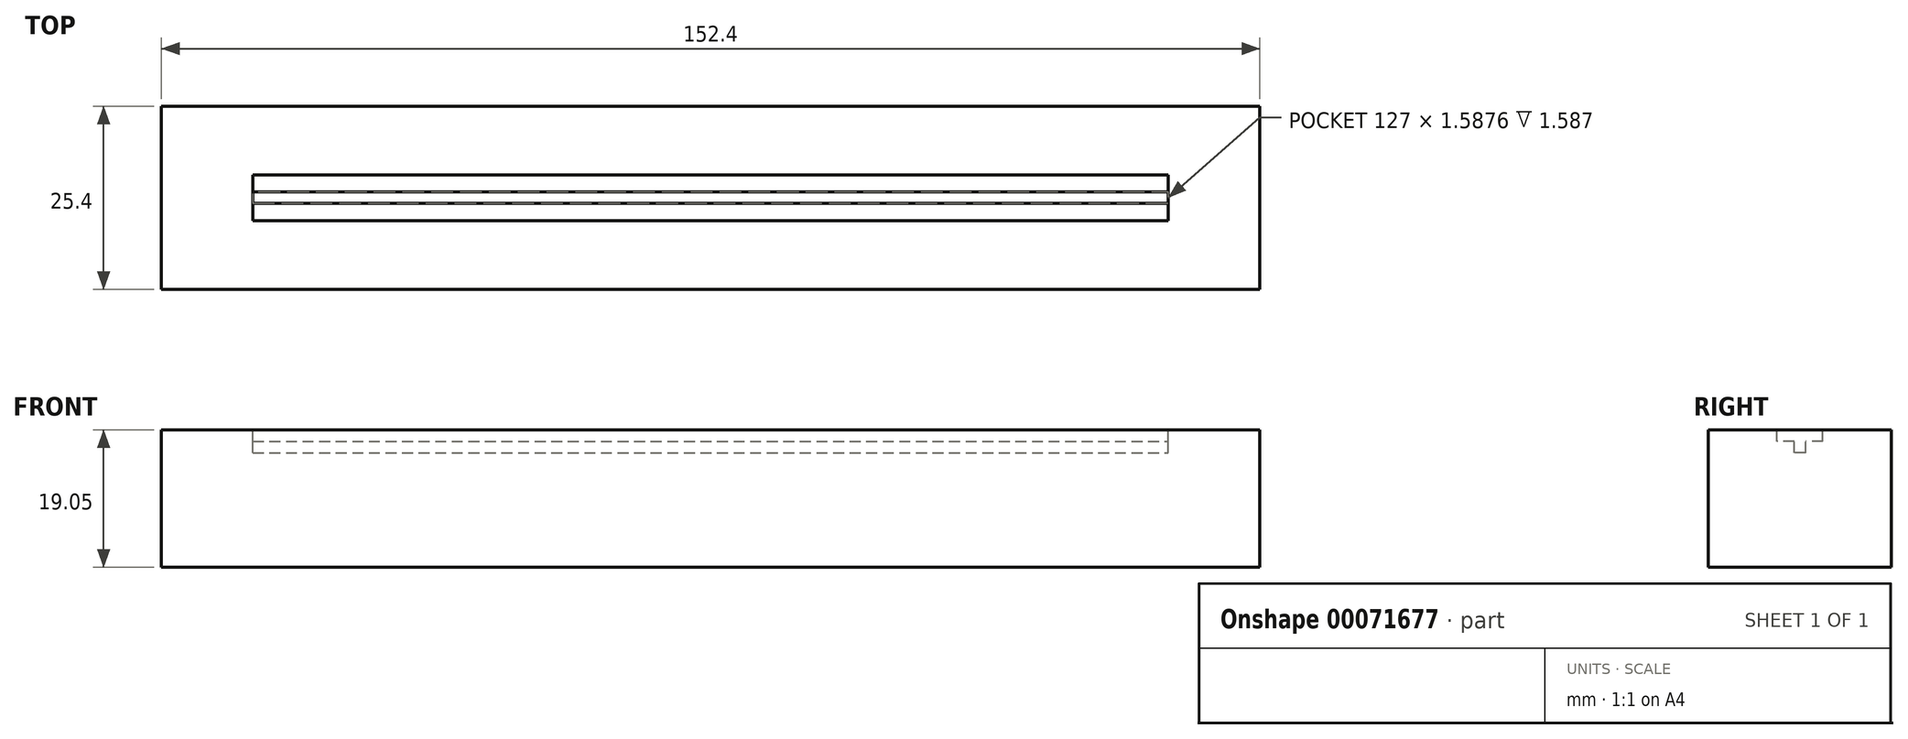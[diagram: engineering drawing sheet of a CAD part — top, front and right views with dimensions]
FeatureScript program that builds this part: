
annotation { "Feature Type Name" : "Feature", "Feature Type Description" : "" }
export const myFeature = defineFeature(function(context is Context, id is Id, definition is map)
    precondition{}
    {
        {
            var Q0;
            Q0=qCreatedBy(makeId("Top.planeOp"),FACE);
            var sketch = newSketch(context, id + "F0", { "sketchPlane" : qUnion([Q0])});
            skLineSegment(sketch, "E0.bottom", {"start": v(0, 0) * mm, "end": v(152.4, 0) * mm});
            skLineSegment(sketch, "E0.top", {"start": v(0, 25.4) * mm, "end": v(152.4, 25.4) * mm});
            skLineSegment(sketch, "E0.left", {"start": v(0, 0) * mm, "end": v(0, 25.4) * mm});
            skLineSegment(sketch, "E0.right", {"start": v(152.4, 0) * mm, "end": v(152.4, 25.4) * mm});
            skSolve(sketch);
        }
        {
            var Q0;
            Q0=qSketchRegion(id+"F0",true);
            extrude(context, id + "F1", {"entities" : qUnion([Q0]), "depth" : 19.05 * mm});
        }
        {
            var Q0;
            Q0=makeQuery(id+"F1.opExtrude","CAP_FACE",FACE,{"disambiguationData":[OSD([sQuery(id+"F0.wireOp",EDGE,"E0.bottom"),sQuery(id+"F0.wireOp",EDGE,"E0.top"),sQuery(id+"F0.wireOp",EDGE,"E0.left"),sQuery(id+"F0.wireOp",EDGE,"E0.right")])],"isStart":false});
            var sketch = newSketch(context, id + "F2", { "sketchPlane" : qUnion([Q0])});
            skLineSegment(sketch, "E1", {"start": v(12.7, 9.53) * mm, "end": v(139.7, 9.53) * mm});
            skLineSegment(sketch, "E2", {"start": v(139.7, 9.53) * mm, "end": v(139.7, 15.88) * mm});
            skLineSegment(sketch, "E3", {"start": v(139.7, 15.88) * mm, "end": v(12.7, 15.88) * mm});
            skLineSegment(sketch, "E4", {"start": v(12.7, 15.88) * mm, "end": v(12.7, 9.53) * mm});
            skSolve(sketch);
        }
        {
            var Q0;
            Q0=qSketchRegion(id+"F2",true);
            extrude(context, id + "F3", {"entities" : qUnion([Q0]), "operationType" : NewBodyOperationType.REMOVE, "oppositeDirection" : true, "depth" : 1.59 * mm});
        }
        {
            var Q0;
            Q0=makeQuery(id+"F3.boolean.opBoolean","COPY",FACE,{"derivedFrom":makeQuery(id+"F3.opExtrude","CAP_FACE",FACE,{"disambiguationData":[OSD([sQuery(id+"F2.wireOp",EDGE,"E1"),sQuery(id+"F2.wireOp",EDGE,"E2"),sQuery(id+"F2.wireOp",EDGE,"E3"),sQuery(id+"F2.wireOp",EDGE,"E4")])],"isStart":false})});
            var sketch = newSketch(context, id + "F4", { "sketchPlane" : qUnion([Q0])});
            skLineSegment(sketch, "E5", {"start": v(12.7, 11.9) * mm, "end": v(139.7, 11.9) * mm});
            skLineSegment(sketch, "E6", {"start": v(12.7, 13.5) * mm, "end": v(139.7, 13.5) * mm});
            skLineSegment(sketch, "E7", {"start": v(139.7, 13.5) * mm, "end": v(139.7, 11.9) * mm});
            skLineSegment(sketch, "E8", {"start": v(12.7, 13.5) * mm, "end": v(12.7, 11.9) * mm});
            skSolve(sketch);
        }
        {
            var Q0;
            Q0=qSketchRegion(id+"F4",true);
            extrude(context, id + "F5", {"entities" : qUnion([Q0]), "operationType" : NewBodyOperationType.REMOVE, "oppositeDirection" : true, "depth" : 1.59 * mm});
        }
    });
